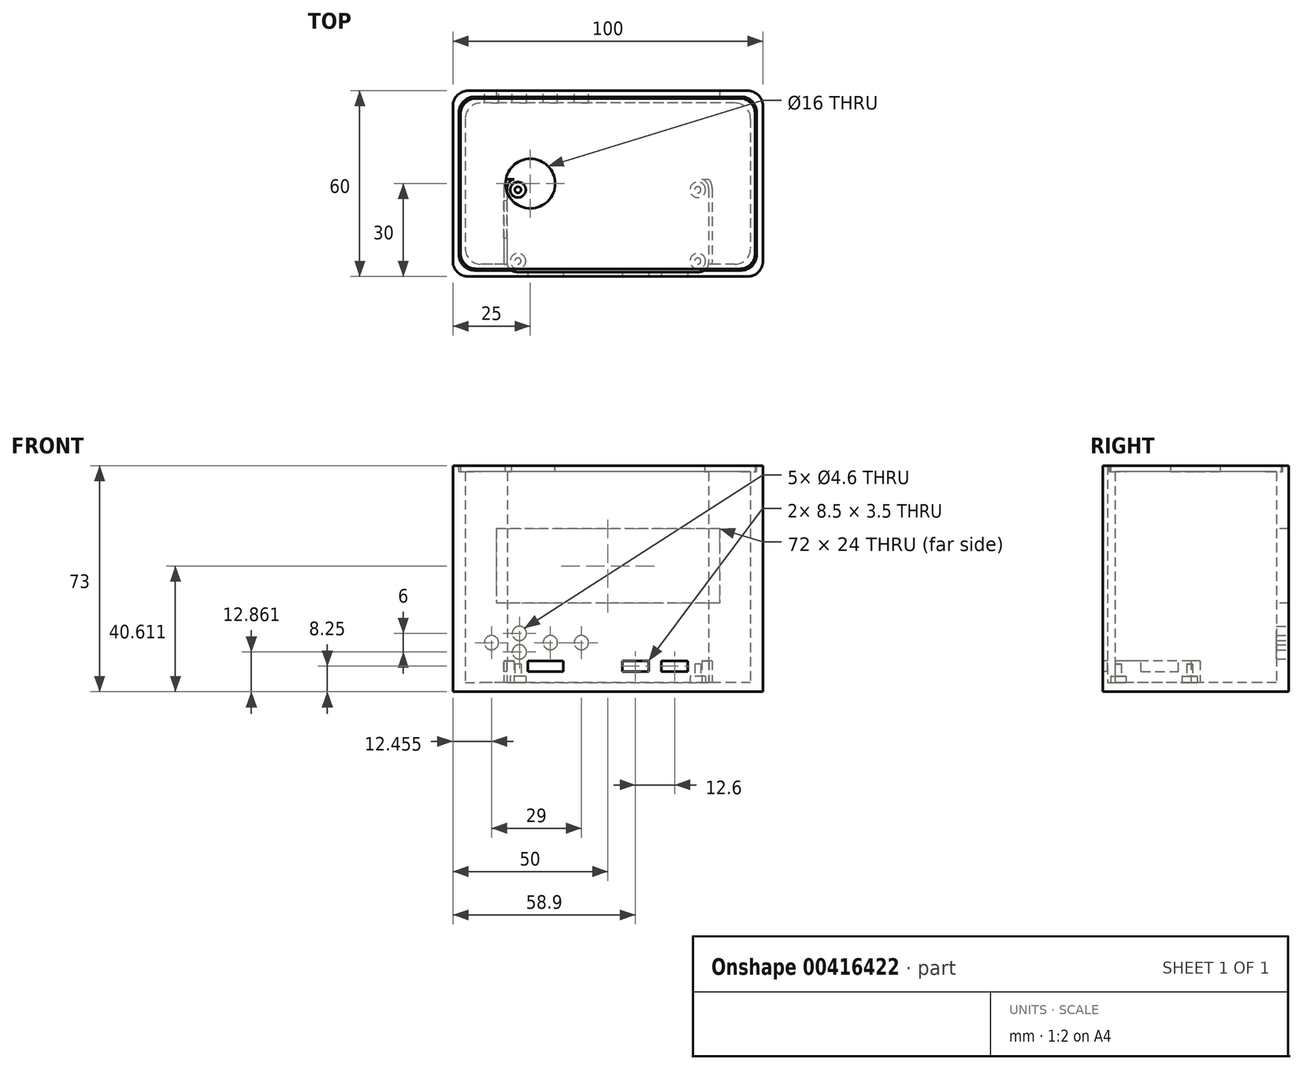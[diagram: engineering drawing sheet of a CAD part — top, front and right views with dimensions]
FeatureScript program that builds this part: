
annotation { "Feature Type Name" : "Feature", "Feature Type Description" : "" }
export const myFeature = defineFeature(function(context is Context, id is Id, definition is map)
    precondition{}
    {
        {
            var Q0;
            Q0=qCreatedBy(makeId("Top.planeOp"),FACE);
            var sketch = newSketch(context, id + "F0", { "sketchPlane" : qUnion([Q0])});
            skLineSegment(sketch, "E0.bottom", {"start": v(45, -30) * mm, "end": v(-45, -30) * mm});
            skLineSegment(sketch, "E0.top", {"start": v(45, 30) * mm, "end": v(-45, 30) * mm});
            skLineSegment(sketch, "E0.left", {"start": v(50, -25) * mm, "end": v(50, 25) * mm});
            skLineSegment(sketch, "E0.right", {"start": v(-50, -25) * mm, "end": v(-50, 25) * mm});
            skPoint(sketch, "E0.middle", {"position": v(0, 0) * mm});
            skPoint(sketch, "E1.visualSharp", {"position": v(-50, -30) * mm});
            skArc(sketch, "E1.filletArc", {"start": v(-50, -25) * mm, "mid": v(-48.54, -28.54) * mm, "end": v(-45, -30) * mm});
            skPoint(sketch, "E2.visualSharp", {"position": v(50, -30) * mm});
            skArc(sketch, "E2.filletArc", {"start": v(45, -30) * mm, "mid": v(48.54, -28.54) * mm, "end": v(50, -25) * mm});
            skPoint(sketch, "E3.visualSharp", {"position": v(50, 30) * mm});
            skArc(sketch, "E3.filletArc", {"start": v(50, 25) * mm, "mid": v(48.54, 28.54) * mm, "end": v(45, 30) * mm});
            skPoint(sketch, "E4.visualSharp", {"position": v(-50, 30) * mm});
            skArc(sketch, "E4.filletArc", {"start": v(-45, 30) * mm, "mid": v(-48.54, 28.54) * mm, "end": v(-50, 25) * mm});
            skSolve(sketch);
        }
        {
            var Q0;
            Q0=makeQuery(id+"F0.imprint","IMPRINT",FACE,{"disambiguationData":[TD([[makeQuery(id+"F0.imprint","IMPRINT",EDGE,{"derivedFrom":sQuery(id+"F0.wireOp",EDGE,"E0.bottom")}),-1.0]])]});
            extrude(context, id + "F1", {"entities" : qUnion([Q0]), "depth" : 3 * mm});
        }
        {
            var Q0;
            Q0=makeQuery(id+"F1.opExtrude","CAP_FACE",FACE,{"disambiguationData":[OSD([sQuery(id+"F0.wireOp",EDGE,"E0.bottom"),sQuery(id+"F0.wireOp",EDGE,"E0.top"),sQuery(id+"F0.wireOp",EDGE,"E0.left"),sQuery(id+"F0.wireOp",EDGE,"E0.right"),sQuery(id+"F0.wireOp",EDGE,"E1.filletArc"),sQuery(id+"F0.wireOp",EDGE,"E2.filletArc"),sQuery(id+"F0.wireOp",EDGE,"E3.filletArc"),sQuery(id+"F0.wireOp",EDGE,"E4.filletArc")])],"isStart":false});
            var sketch = newSketch(context, id + "F2", { "sketchPlane" : qUnion([Q0])});
            skLineSegment(sketch, "E5.rect.bottom", {"start": v(32.5, -28.5) * mm, "end": v(-32.5, -28.5) * mm, "construction": true});
            skLineSegment(sketch, "E5.rect.top", {"start": v(32.5, 1.5) * mm, "end": v(-32.5, 1.5) * mm, "construction": true});
            skLineSegment(sketch, "E5.rect.right", {"start": v(-32.5, -28.5) * mm, "end": v(-32.5, 1.5) * mm, "construction": true});
            skPoint(sketch, "E5.rect.middle", {"position": v(0, -13.5) * mm});
            skLineSegment(sketch, "E6", {"start": v(-20.1, -28.5) * mm, "end": v(-20.1, 1.5) * mm, "construction": true});
            skLineSegment(sketch, "E7", {"start": v(-29, -28.5) * mm, "end": v(-29, 1.5) * mm, "construction": true});
            skLineSegment(sketch, "E8", {"start": v(0, 1.5) * mm, "end": v(0, -28.5) * mm, "construction": true});
            skLineSegment(sketch, "E9.MirrorCS", {"start": v(29, -28.5) * mm, "end": v(29, 1.5) * mm, "construction": true});
            skLineSegment(sketch, "E10", {"start": v(32.5, -13.5) * mm, "end": v(-32.5, -13.5) * mm, "construction": true});
            skLineSegment(sketch, "E11", {"start": v(-32.5, -25) * mm, "end": v(32.5, -25) * mm, "construction": true});
            skLineSegment(sketch, "E12.MirrorCS", {"start": v(-32.5, -2) * mm, "end": v(32.5, -2) * mm, "construction": true});
            skPoint(sketch, "E13", {"position": v(-29, -2) * mm});
            skPoint(sketch, "E14", {"position": v(29, -2) * mm});
            skPoint(sketch, "E15", {"position": v(29, -25) * mm});
            skPoint(sketch, "E16", {"position": v(-29, -25) * mm});
            skLineSegment(sketch, "E17", {"start": v(8.9, 1.5) * mm, "end": v(8.9, -28.5) * mm, "construction": true});
            skLineSegment(sketch, "E18", {"start": v(21.5, 1.5) * mm, "end": v(21.5, -28.5) * mm, "construction": true});
            skArc(sketch, "E19", {"start": v(-32.5, -1.5) * mm, "mid": v(-31.62, 0.62) * mm, "end": v(-29.5, 1.5) * mm});
            skArc(sketch, "E20.MirrorCS", {"start": v(32.5, -1.5) * mm, "mid": v(31.62, 0.62) * mm, "end": v(29.5, 1.5) * mm});
            skArc(sketch, "E21.MirrorCS", {"start": v(-32.5, -25.5) * mm, "mid": v(-31.62, -27.62) * mm, "end": v(-29.5, -28.5) * mm});
            skArc(sketch, "E22.MirrorCS", {"start": v(32.5, -25.5) * mm, "mid": v(31.62, -27.62) * mm, "end": v(29.5, -28.5) * mm});
            skLineSegment(sketch, "E23", {"start": v(-32.5, -1.5) * mm, "end": v(-32.5, -25.5) * mm});
            skLineSegment(sketch, "E24", {"start": v(-29.5, -28.5) * mm, "end": v(29.5, -28.5) * mm});
            skLineSegment(sketch, "E25", {"start": v(-29.5, 1.5) * mm, "end": v(29.5, 1.5) * mm});
            skLineSegment(sketch, "E26", {"start": v(32.5, -1.5) * mm, "end": v(32.5, -25.5) * mm});
            skLineSegment(sketch, "E27", {"start": v(-32.5, -11.6) * mm, "end": v(32.5, -11.6) * mm, "construction": true});
            skArc(sketch, "E28.0", {"start": v(-33.62, -1.5) * mm, "mid": v(-32.3, 1.68) * mm, "end": v(-29.12, 3) * mm});
            skLineSegment(sketch, "E28.1", {"start": v(-33.62, -1.5) * mm, "end": v(-33.62, -25.5) * mm});
            skLineSegment(sketch, "E28.2", {"start": v(-29.12, 3) * mm, "end": v(29.88, 3) * mm});
            skArc(sketch, "E28.3", {"start": v(-33.62, -25.5) * mm, "mid": v(-32.3, -28.68) * mm, "end": v(-29.12, -30) * mm});
            skArc(sketch, "E28.4", {"start": v(33.62, -1.5) * mm, "mid": v(32.58, 1.44) * mm, "end": v(29.88, 3) * mm});
            skLineSegment(sketch, "E28.5", {"start": v(33.62, -1.5) * mm, "end": v(33.62, -25.5) * mm});
            skArc(sketch, "E28.6", {"start": v(33.62, -25.5) * mm, "mid": v(32.3, -28.68) * mm, "end": v(29.12, -30) * mm});
            skLineSegment(sketch, "E28.7", {"start": v(-29.12, -30) * mm, "end": v(29.12, -30) * mm});
            skLineSegment(sketch, "E29.trimOffspring", {"start": v(0, -13.5) * mm, "end": v(0, -30) * mm, "construction": true});
            skSolve(sketch);
        }
        {
            var Q0;
            Q0 = qSketchRegion(id + "F2", true);
            extrude(context, id + "F3", {"entities" : qUnion([Q0]), "operationType" : NewBodyOperationType.ADD, "depth" : 7 * mm});
        }
        {
            var Q0;
            Q0=makeQuery(id+"F3.boolean.opBoolean","MERGE",FACE,{"derivedFrom":[makeQuery(id+"F1.opExtrude","SWEPT_FACE",FACE,{"disambiguationData":[OSD([sQuery(id+"F0.wireOp",EDGE,"E0.bottom")])]}),makeQuery(id+"F3.opExtrude","SWEPT_FACE",FACE,{"disambiguationData":[OSD([sQuery(id+"F2.wireOp",EDGE,"E28.7")])]})]});
            var sketch = newSketch(context, id + "F4", { "sketchPlane" : qUnion([Q0])});
            skPoint(sketch, "E30.0", {"position": v(-20.1, 3) * mm});
            skPoint(sketch, "E30.1", {"position": v(8.9, 3) * mm});
            skPoint(sketch, "E30.2", {"position": v(21.5, 3) * mm});
            skLineSegment(sketch, "E31", {"start": v(-20.1, 3) * mm, "end": v(-20.1, 10.5) * mm, "construction": true});
            skLineSegment(sketch, "E32", {"start": v(8.9, 3) * mm, "end": v(8.9, 10.5) * mm, "construction": true});
            skLineSegment(sketch, "E33", {"start": v(21.5, 3) * mm, "end": v(21.5, 10.5) * mm, "construction": true});
            skLineSegment(sketch, "E34.rect.bottom", {"start": v(-14.35, 6.5) * mm, "end": v(-25.85, 6.5) * mm});
            skLineSegment(sketch, "E34.rect.top", {"start": v(-14.35, 10) * mm, "end": v(-25.85, 10) * mm});
            skLineSegment(sketch, "E34.rect.left", {"start": v(-14.35, 6.5) * mm, "end": v(-14.35, 10) * mm});
            skLineSegment(sketch, "E34.rect.right", {"start": v(-25.85, 6.5) * mm, "end": v(-25.85, 10) * mm});
            skPoint(sketch, "E34.rect.middle", {"position": v(-20.1, 8.25) * mm});
            skLineSegment(sketch, "E35.rect.bottom", {"start": v(13.15, 6.5) * mm, "end": v(4.65, 6.5) * mm});
            skLineSegment(sketch, "E35.rect.top", {"start": v(13.15, 10) * mm, "end": v(4.65, 10) * mm});
            skLineSegment(sketch, "E35.rect.left", {"start": v(13.15, 6.5) * mm, "end": v(13.15, 10) * mm});
            skLineSegment(sketch, "E35.rect.right", {"start": v(4.65, 6.5) * mm, "end": v(4.65, 10) * mm});
            skPoint(sketch, "E35.rect.middle", {"position": v(8.9, 8.25) * mm});
            skLineSegment(sketch, "E36.rect.bottom", {"start": v(25.75, 6.5) * mm, "end": v(17.25, 6.5) * mm});
            skLineSegment(sketch, "E36.rect.top", {"start": v(25.75, 10) * mm, "end": v(17.25, 10) * mm});
            skLineSegment(sketch, "E36.rect.left", {"start": v(25.75, 6.5) * mm, "end": v(25.75, 10) * mm});
            skLineSegment(sketch, "E36.rect.right", {"start": v(17.25, 6.5) * mm, "end": v(17.25, 10) * mm});
            skPoint(sketch, "E36.rect.middle", {"position": v(21.5, 8.25) * mm});
            skSolve(sketch);
        }
        {
            var Q0;
            Q0 = qSketchRegion(id + "F4", true);
            extrude(context, id + "F5", {"entities" : qUnion([Q0]), "operationType" : NewBodyOperationType.REMOVE, "endBound" : BoundingType.UP_TO_NEXT, "oppositeDirection" : true, "depth" : 25 * mm});
        }
        {
            var Q0;
            Q0=makeQuery(id+"F2.imprint","IMPRINT",FACE,{"disambiguationData":[TD([[makeQuery(id+"F2.imprint","IMPRINT",EDGE,{"derivedFrom":sQuery(id+"F2.wireOp",EDGE,"E19")}),-1.0]])]});
            var sketch = newSketch(context, id + "F6", { "sketchPlane" : qUnion([Q0])});
            skPoint(sketch, "E37.0", {"position": v(-29, -2) * mm});
            skCircle(sketch, "E38", {"center": v(-29, -2) * mm, "radius": 2.5 * mm});
            skCircle(sketch, "E39.MirrorC", {"center": v(29, -2) * mm, "radius": 2.5 * mm});
            skCircle(sketch, "E40.MirrorC", {"center": v(29, -25) * mm, "radius": 2.5 * mm});
            skCircle(sketch, "E41.MirrorC", {"center": v(-29, -25) * mm, "radius": 2.5 * mm});
            skSolve(sketch);
        }
        {
            var Q0;
            Q0 = qSketchRegion(id + "F6", true);
            extrude(context, id + "F7", {"entities" : qUnion([Q0]), "operationType" : NewBodyOperationType.ADD, "depth" : 2 * mm});
        }
        {
            var Q0;
            Q0=makeQuery(id+"F7.opExtrude","CAP_FACE",FACE,{"disambiguationData":[OSD([sQuery(id+"F6.wireOp",EDGE,"E38")])],"isStart":false});
            var sketch = newSketch(context, id + "F8", { "sketchPlane" : qUnion([Q0])});
            skPoint(sketch, "E42.0", {"position": v(-29, -2) * mm});
            skCircle(sketch, "E43", {"center": v(-29, -2) * mm, "radius": 1 * mm});
            skCircle(sketch, "E44.MirrorC", {"center": v(29, -2) * mm, "radius": 1 * mm});
            skCircle(sketch, "E45.MirrorC", {"center": v(29, -25) * mm, "radius": 1 * mm});
            skCircle(sketch, "E46.MirrorC", {"center": v(-29, -25) * mm, "radius": 1 * mm});
            skSolve(sketch);
        }
        {
            var Q0;
            Q0 = qSketchRegion(id + "F8", true);
            extrude(context, id + "F9", {"entities" : qUnion([Q0]), "operationType" : NewBodyOperationType.ADD, "depth" : 4 * mm});
        }
        {
            var Q0;
            Q0=makeQuery(id+"F3.opExtrude","SWEPT_FACE",FACE,{"disambiguationData":[OSD([sQuery(id+"F2.wireOp",EDGE,"E28.1")])]});
            var sketch = newSketch(context, id + "F10", { "sketchPlane" : qUnion([Q0])});
            skPoint(sketch, "E47.0", {"position": v(11.6, 3) * mm});
            skLineSegment(sketch, "E48", {"start": v(11.6, 3) * mm, "end": v(11.6, 11.3) * mm, "construction": true});
            skLineSegment(sketch, "E49.rect.bottom", {"start": v(17.65, 6.5) * mm, "end": v(5.55, 6.5) * mm});
            skLineSegment(sketch, "E49.rect.top", {"start": v(17.65, 10) * mm, "end": v(5.55, 10) * mm});
            skLineSegment(sketch, "E49.rect.left", {"start": v(17.65, 6.5) * mm, "end": v(17.65, 10) * mm});
            skLineSegment(sketch, "E49.rect.right", {"start": v(5.55, 6.5) * mm, "end": v(5.55, 10) * mm});
            skPoint(sketch, "E49.rect.middle", {"position": v(11.6, 8.25) * mm});
            skSolve(sketch);
        }
        {
            var Q0;
            Q0 = qSketchRegion(id + "F10", true);
            extrude(context, id + "F11", {"entities" : qUnion([Q0]), "operationType" : NewBodyOperationType.REMOVE, "endBound" : BoundingType.UP_TO_NEXT, "oppositeDirection" : true, "depth" : 25 * mm});
        }
        {
            var Q0;
            Q0=makeQuery(id+"F2.imprint","IMPRINT",FACE,{"disambiguationData":[TD([[makeQuery(id+"F2.imprint","IMPRINT",EDGE,{"derivedFrom":sQuery(id+"F2.wireOp",EDGE,"E28.0")}),1.0]])]});
            var sketch = newSketch(context, id + "F12", { "sketchPlane" : qUnion([Q0])});
            skLineSegment(sketch, "E50.bottom", {"start": v(45, 30) * mm, "end": v(-45, 30) * mm});
            skLineSegment(sketch, "E50.top", {"start": v(45, -30) * mm, "end": v(29.12, -30) * mm});
            skLineSegment(sketch, "E50.left", {"start": v(50, 25) * mm, "end": v(50, -25) * mm});
            skLineSegment(sketch, "E50.right", {"start": v(-50, 25) * mm, "end": v(-50, -25) * mm});
            skPoint(sketch, "E50.middle", {"position": v(0, 0) * mm});
            skPoint(sketch, "E51.visualSharp", {"position": v(50, 30) * mm});
            skArc(sketch, "E51.filletArc", {"start": v(50, 25) * mm, "mid": v(48.54, 28.54) * mm, "end": v(45, 30) * mm});
            skPoint(sketch, "E52.visualSharp", {"position": v(50, -30) * mm});
            skArc(sketch, "E52.filletArc", {"start": v(45, -30) * mm, "mid": v(48.54, -28.54) * mm, "end": v(50, -25) * mm});
            skPoint(sketch, "E53.visualSharp", {"position": v(-50, -30) * mm});
            skArc(sketch, "E53.filletArc", {"start": v(-50, -25) * mm, "mid": v(-48.54, -28.54) * mm, "end": v(-45, -30) * mm});
            skPoint(sketch, "E54.visualSharp", {"position": v(-50, 30) * mm});
            skArc(sketch, "E54.filletArc", {"start": v(-45, 30) * mm, "mid": v(-48.54, 28.54) * mm, "end": v(-50, 25) * mm});
            skLineSegment(sketch, "E55.bottom", {"start": v(41, 26) * mm, "end": v(-41, 26) * mm});
            skLineSegment(sketch, "E55.top", {"start": v(41, -26) * mm, "end": v(33.6, -26) * mm});
            skLineSegment(sketch, "E55.left", {"start": v(46, 21) * mm, "end": v(46, -21) * mm});
            skLineSegment(sketch, "E55.right", {"start": v(-46, 21) * mm, "end": v(-46, -21) * mm});
            skPoint(sketch, "E56.visualSharp", {"position": v(46, 26) * mm});
            skArc(sketch, "E56.filletArc", {"start": v(46, 21) * mm, "mid": v(44.54, 24.54) * mm, "end": v(41, 26) * mm});
            skPoint(sketch, "E57.visualSharp", {"position": v(46, -26) * mm});
            skArc(sketch, "E57.filletArc", {"start": v(41, -26) * mm, "mid": v(44.54, -24.54) * mm, "end": v(46, -21) * mm});
            skPoint(sketch, "E58.visualSharp", {"position": v(-46, -26) * mm});
            skArc(sketch, "E58.filletArc", {"start": v(-46, -21) * mm, "mid": v(-44.54, -24.54) * mm, "end": v(-41, -26) * mm});
            skPoint(sketch, "E59.visualSharp", {"position": v(-46, 26) * mm});
            skArc(sketch, "E59.filletArc", {"start": v(-41, 26) * mm, "mid": v(-44.54, 24.54) * mm, "end": v(-46, 21) * mm});
            skLineSegment(sketch, "E60.trimOffspring", {"start": v(-29.12, -30) * mm, "end": v(-45, -30) * mm});
            skLineSegment(sketch, "E61.trimOffspring", {"start": v(-33.6, -26) * mm, "end": v(-41, -26) * mm});
            skArc(sketch, "E62.0", {"start": v(-33.6, -26) * mm, "mid": v(-32.12, -28.85) * mm, "end": v(-29.12, -30) * mm});
            skArc(sketch, "E63.0", {"start": v(33.6, -26) * mm, "mid": v(32.12, -28.85) * mm, "end": v(29.12, -30) * mm});
            skPoint(sketch, "E64.orphan", {"position": v(33.62, -25.5) * mm});
            skPoint(sketch, "E65.orphan", {"position": v(-33.62, -25.5) * mm});
            skSolve(sketch);
        }
        {
            var Q0;
            Q0 = qSketchRegion(id + "F12", true);
            var Q1;
            {var subQ0=sQuery(id+"F2.wireOp",EDGE,"E23");var subQ2=sQuery(id+"F2.wireOp",EDGE,"E28.7");var subQ4=sQuery(id+"F2.wireOp",EDGE,"E21.MirrorCS");var subQ5=makeQuery(id+"F3.opExtrude","SWEPT_FACE",FACE,{"disambiguationData":[OSD([subQ4])]});var subQ6=sQuery(id+"F2.wireOp",EDGE,"E24");var subQ9=sQuery(id+"F2.wireOp",EDGE,"E28.1");var subQ12=sQuery(id+"F2.wireOp",EDGE,"E28.3");var subQ14=sQuery(id+"F2.wireOp",EDGE,"E26");var subQ15=sQuery(id+"F2.wireOp",EDGE,"E25");var subQ16=sQuery(id+"F2.wireOp",EDGE,"E22.MirrorCS");var subQ17=sQuery(id+"F2.wireOp",EDGE,"E28.0");var subQ18=sQuery(id+"F2.wireOp",EDGE,"E19");var subQ19=sQuery(id+"F2.wireOp",EDGE,"E20.MirrorCS");var subQ20=sQuery(id+"F2.wireOp",EDGE,"E28.2");var subQ21=sQuery(id+"F2.wireOp",EDGE,"E28.4");var subQ22=sQuery(id+"F2.wireOp",EDGE,"E28.5");var subQ23=sQuery(id+"F2.wireOp",EDGE,"E28.6");Q1=makeQuery(id+"F11.boolean.opBoolean","SPLIT",FACE,{"disambiguationData":[TD([subQ5])],"derivedFrom":makeQuery(id+"F5.boolean.opBoolean","SPLIT",FACE,{"disambiguationData":[TD([makeQuery(id+"F3.opExtrude","SWEPT_FACE",FACE,{"disambiguationData":[OSD([subQ18])]})])],"derivedFrom":makeQuery(id+"F3.opExtrude","CAP_FACE",FACE,{"disambiguationData":[OSD([subQ18,subQ19,subQ4,subQ16,subQ0,subQ6,subQ15,subQ14,subQ17,subQ9,subQ20,subQ12,subQ21,subQ22,subQ23,subQ2])],"isStart":false})})});}
            extrude(context, id + "F13", {"entities" : qUnion([Q0]), "operationType" : NewBodyOperationType.ADD, "endBound" : BoundingType.UP_TO_SURFACE, "endBoundEntityFace" : qUnion([Q1]), "depth" : 66 * mm});
        }
        {
            var Q0;
            {var subQ0=sQuery(id+"F2.wireOp",EDGE,"E23");var subQ2=sQuery(id+"F2.wireOp",EDGE,"E28.7");var subQ4=sQuery(id+"F2.wireOp",EDGE,"E21.MirrorCS");var subQ5=makeQuery(id+"F3.opExtrude","SWEPT_FACE",FACE,{"disambiguationData":[OSD([subQ4])]});var subQ6=sQuery(id+"F2.wireOp",EDGE,"E24");var subQ9=sQuery(id+"F2.wireOp",EDGE,"E28.1");var subQ12=sQuery(id+"F2.wireOp",EDGE,"E28.3");var subQ14=sQuery(id+"F2.wireOp",EDGE,"E26");var subQ16=sQuery(id+"F2.wireOp",EDGE,"E25");var subQ18=sQuery(id+"F2.wireOp",EDGE,"E22.MirrorCS");var subQ20=sQuery(id+"F2.wireOp",EDGE,"E28.0");var subQ22=sQuery(id+"F2.wireOp",EDGE,"E19");var subQ23=makeQuery(id+"F3.opExtrude","SWEPT_FACE",FACE,{"disambiguationData":[OSD([subQ22])]});var subQ24=sQuery(id+"F2.wireOp",EDGE,"E20.MirrorCS");var subQ27=sQuery(id+"F2.wireOp",EDGE,"E28.2");var subQ29=sQuery(id+"F2.wireOp",EDGE,"E28.4");var subQ31=sQuery(id+"F2.wireOp",EDGE,"E28.5");var subQ33=sQuery(id+"F2.wireOp",EDGE,"E28.6");var subQ35=makeQuery(id+"F5.boolean.opBoolean","SPLIT",FACE,{"disambiguationData":[TD([subQ23])],"derivedFrom":makeQuery(id+"F3.opExtrude","CAP_FACE",FACE,{"disambiguationData":[OSD([subQ22,subQ24,subQ4,subQ18,subQ0,subQ6,subQ16,subQ14,subQ20,subQ9,subQ27,subQ12,subQ29,subQ31,subQ33,subQ2])],"isStart":false})});Q0=makeQuery(id+"F13.boolean.opBoolean","MERGE",FACE,{"derivedFrom":[makeQuery(id+"F11.boolean.opBoolean","SPLIT",FACE,{"disambiguationData":[TD([subQ23])],"derivedFrom":subQ35}),makeQuery(id+"F11.boolean.opBoolean","SPLIT",FACE,{"disambiguationData":[TD([subQ5])],"derivedFrom":subQ35}),makeQuery(id+"F13.opExtrude","CAP_FACE",FACE,{"disambiguationData":[OSD([sQuery(id+"F12.wireOp",EDGE,"E50.bottom"),sQuery(id+"F12.wireOp",EDGE,"E50.top"),sQuery(id+"F12.wireOp",EDGE,"E50.left"),sQuery(id+"F12.wireOp",EDGE,"E50.right"),sQuery(id+"F12.wireOp",EDGE,"E51.filletArc"),sQuery(id+"F12.wireOp",EDGE,"E52.filletArc"),sQuery(id+"F12.wireOp",EDGE,"E53.filletArc"),sQuery(id+"F12.wireOp",EDGE,"E54.filletArc"),sQuery(id+"F12.wireOp",EDGE,"E55.bottom"),sQuery(id+"F12.wireOp",EDGE,"E55.top"),sQuery(id+"F12.wireOp",EDGE,"E55.left"),sQuery(id+"F12.wireOp",EDGE,"E55.right"),sQuery(id+"F12.wireOp",EDGE,"E56.filletArc"),sQuery(id+"F12.wireOp",EDGE,"E57.filletArc"),sQuery(id+"F12.wireOp",EDGE,"E58.filletArc"),sQuery(id+"F12.wireOp",EDGE,"E59.filletArc"),sQuery(id+"F12.wireOp",EDGE,"E60.trimOffspring"),sQuery(id+"F12.wireOp",EDGE,"E61.trimOffspring"),sQuery(id+"F12.wireOp",EDGE,"E62.0"),sQuery(id+"F12.wireOp",EDGE,"E63.0")])],"isStart":false})]});}
            var sketch = newSketch(context, id + "F14", { "sketchPlane" : qUnion([Q0])});
            skLineSegment(sketch, "E66.bottom", {"start": v(45, 30) * mm, "end": v(-45, 30) * mm});
            skLineSegment(sketch, "E66.top", {"start": v(45, -30) * mm, "end": v(-45, -30) * mm});
            skLineSegment(sketch, "E66.left", {"start": v(50, 25) * mm, "end": v(50, -25) * mm});
            skLineSegment(sketch, "E66.right", {"start": v(-50, 25) * mm, "end": v(-50, -25) * mm});
            skPoint(sketch, "E66.middle", {"position": v(0, 0) * mm});
            skPoint(sketch, "E67.visualSharp", {"position": v(50, 30) * mm});
            skArc(sketch, "E67.filletArc", {"start": v(50, 25) * mm, "mid": v(48.54, 28.54) * mm, "end": v(45, 30) * mm});
            skPoint(sketch, "E68.visualSharp", {"position": v(-50, 30) * mm});
            skArc(sketch, "E68.filletArc", {"start": v(-45, 30) * mm, "mid": v(-48.54, 28.54) * mm, "end": v(-50, 25) * mm});
            skPoint(sketch, "E69.visualSharp", {"position": v(-50, -30) * mm});
            skArc(sketch, "E69.filletArc", {"start": v(-50, -25) * mm, "mid": v(-48.54, -28.54) * mm, "end": v(-45, -30) * mm});
            skPoint(sketch, "E70.visualSharp", {"position": v(50, -30) * mm});
            skArc(sketch, "E70.filletArc", {"start": v(45, -30) * mm, "mid": v(48.54, -28.54) * mm, "end": v(50, -25) * mm});
            skLineSegment(sketch, "E71.bottom", {"start": v(41, 26) * mm, "end": v(-41, 26) * mm});
            skLineSegment(sketch, "E71.left", {"start": v(46, 21) * mm, "end": v(46, -21) * mm});
            skLineSegment(sketch, "E71.right", {"start": v(-46, 21) * mm, "end": v(-46, -21) * mm});
            skPoint(sketch, "E72.visualSharp", {"position": v(46, 26) * mm});
            skArc(sketch, "E72.filletArc", {"start": v(46, 21) * mm, "mid": v(44.54, 24.54) * mm, "end": v(41, 26) * mm});
            skPoint(sketch, "E73.visualSharp", {"position": v(46, -26) * mm});
            skArc(sketch, "E73.filletArc", {"start": v(41, -26) * mm, "mid": v(44.54, -24.54) * mm, "end": v(46, -21) * mm});
            skPoint(sketch, "E74.visualSharp", {"position": v(-46, -26) * mm});
            skArc(sketch, "E74.filletArc", {"start": v(-46, -21) * mm, "mid": v(-44.54, -24.54) * mm, "end": v(-41, -26) * mm});
            skPoint(sketch, "E75.visualSharp", {"position": v(-46, 26) * mm});
            skArc(sketch, "E75.filletArc", {"start": v(-41, 26) * mm, "mid": v(-44.54, 24.54) * mm, "end": v(-46, 21) * mm});
            skArc(sketch, "E76", {"start": v(-32.46, -26) * mm, "mid": v(-31.44, -27.8) * mm, "end": v(-29.5, -28.5) * mm});
            skArc(sketch, "E77", {"start": v(29.5, -28.5) * mm, "mid": v(31.44, -27.8) * mm, "end": v(32.46, -26) * mm});
            skLineSegment(sketch, "E78", {"start": v(41, -26) * mm, "end": v(32.46, -26) * mm});
            skLineSegment(sketch, "E79", {"start": v(29.5, -28.5) * mm, "end": v(-29.5, -28.5) * mm});
            skLineSegment(sketch, "E80", {"start": v(-41, -26) * mm, "end": v(-32.46, -26) * mm});
            skSolve(sketch);
        }
        {
            var Q0;
            Q0 = qSketchRegion(id + "F14", true);
            extrude(context, id + "F15", {"entities" : qUnion([Q0]), "operationType" : NewBodyOperationType.ADD, "depth" : 63 * mm});
        }
        {
            var Q0;
            Q0=makeQuery(id+"F15.opExtrude","CAP_FACE",FACE,{"disambiguationData":[OSD([sQuery(id+"F14.wireOp",EDGE,"E66.bottom"),sQuery(id+"F14.wireOp",EDGE,"E66.top"),sQuery(id+"F14.wireOp",EDGE,"E66.left"),sQuery(id+"F14.wireOp",EDGE,"E66.right"),sQuery(id+"F14.wireOp",EDGE,"E67.filletArc"),sQuery(id+"F14.wireOp",EDGE,"E68.filletArc"),sQuery(id+"F14.wireOp",EDGE,"E69.filletArc"),sQuery(id+"F14.wireOp",EDGE,"E70.filletArc"),sQuery(id+"F14.wireOp",EDGE,"E71.bottom"),sQuery(id+"F14.wireOp",EDGE,"E71.left"),sQuery(id+"F14.wireOp",EDGE,"E71.right"),sQuery(id+"F14.wireOp",EDGE,"E72.filletArc"),sQuery(id+"F14.wireOp",EDGE,"E73.filletArc"),sQuery(id+"F14.wireOp",EDGE,"E74.filletArc"),sQuery(id+"F14.wireOp",EDGE,"E75.filletArc"),sQuery(id+"F14.wireOp",EDGE,"E76"),sQuery(id+"F14.wireOp",EDGE,"E77"),sQuery(id+"F14.wireOp",EDGE,"E78"),sQuery(id+"F14.wireOp",EDGE,"E79"),sQuery(id+"F14.wireOp",EDGE,"E80")])],"isStart":false});
            var sketch = newSketch(context, id + "F16", { "sketchPlane" : qUnion([Q0])});
            skLineSegment(sketch, "E81.bottom", {"start": v(43, 28) * mm, "end": v(-43, 28) * mm});
            skLineSegment(sketch, "E81.top", {"start": v(43, -28) * mm, "end": v(-43, -28) * mm});
            skLineSegment(sketch, "E81.left", {"start": v(48, 23) * mm, "end": v(48, -23) * mm});
            skLineSegment(sketch, "E81.right", {"start": v(-48, 23) * mm, "end": v(-48, -23) * mm});
            skPoint(sketch, "E81.middle", {"position": v(0, 0) * mm});
            skPoint(sketch, "E82.visualSharp", {"position": v(-48, -28) * mm});
            skArc(sketch, "E82.filletArc", {"start": v(-48, -23) * mm, "mid": v(-46.54, -26.54) * mm, "end": v(-43, -28) * mm});
            skPoint(sketch, "E83.visualSharp", {"position": v(48, -28) * mm});
            skArc(sketch, "E83.filletArc", {"start": v(43, -28) * mm, "mid": v(46.54, -26.54) * mm, "end": v(48, -23) * mm});
            skPoint(sketch, "E84.visualSharp", {"position": v(48, 28) * mm});
            skArc(sketch, "E84.filletArc", {"start": v(48, 23) * mm, "mid": v(46.54, 26.54) * mm, "end": v(43, 28) * mm});
            skPoint(sketch, "E85.visualSharp", {"position": v(-48, 28) * mm});
            skArc(sketch, "E85.filletArc", {"start": v(-43, 28) * mm, "mid": v(-46.54, 26.54) * mm, "end": v(-48, 23) * mm});
            skSolve(sketch);
        }
        {
            var Q0;
            Q0 = qSketchRegion(id + "F16", true);
            extrude(context, id + "F17", {"entities" : qUnion([Q0]), "operationType" : NewBodyOperationType.REMOVE, "oppositeDirection" : true, "depth" : 2 * mm});
        }
        {
            var Q0;
            Q0=makeQuery(id+"F15.boolean.opBoolean","MERGE",FACE,{"derivedFrom":[makeQuery(id+"F13.opExtrude","SWEPT_FACE",FACE,{"disambiguationData":[OSD([sQuery(id+"F12.wireOp",EDGE,"E55.bottom")])]}),makeQuery(id+"F15.opExtrude","SWEPT_FACE",FACE,{"disambiguationData":[OSD([sQuery(id+"F14.wireOp",EDGE,"E71.bottom")])]})]});
            var sketch = newSketch(context, id + "F18", { "sketchPlane" : qUnion([Q0])});
            skLineSegment(sketch, "E86.bottom", {"start": v(37.47, 56.1) * mm, "end": v(-37.47, 56.1) * mm, "construction": true});
            skLineSegment(sketch, "E86.top", {"start": v(37.47, 25.12) * mm, "end": v(-37.47, 25.12) * mm, "construction": true});
            skLineSegment(sketch, "E86.left", {"start": v(37.47, 56.1) * mm, "end": v(37.47, 25.12) * mm, "construction": true});
            skLineSegment(sketch, "E86.right", {"start": v(-37.47, 56.1) * mm, "end": v(-37.47, 25.12) * mm, "construction": true});
            skPoint(sketch, "E86.middle", {"position": v(0, 40.61) * mm});
            skCircle(sketch, "E87", {"center": v(-37.47, 56.1) * mm, "radius": 3 * mm});
            skCircle(sketch, "E88", {"center": v(37.47, 56.1) * mm, "radius": 3 * mm});
            skCircle(sketch, "E89", {"center": v(37.47, 25.12) * mm, "radius": 3 * mm});
            skCircle(sketch, "E90", {"center": v(-37.47, 25.12) * mm, "radius": 3 * mm});
            skCircle(sketch, "E91", {"center": v(-37.47, 56.1) * mm, "radius": 1.13 * mm});
            skCircle(sketch, "E92", {"center": v(37.47, 56.1) * mm, "radius": 1.13 * mm});
            skCircle(sketch, "E93", {"center": v(37.47, 25.12) * mm, "radius": 1.13 * mm});
            skCircle(sketch, "E94", {"center": v(-37.47, 25.12) * mm, "radius": 1.13 * mm});
            skSolve(sketch);
        }
        {
            var Q0;
            Q0=makeQuery(id+"FcJJ7sOJFXP5bAi_1.boolean.opBoolean","SPLIT",FACE,{"disambiguationData":[TD([makeQuery(id+"F13.opExtrude","SWEPT_FACE",FACE,{"disambiguationData":[OSD([sQuery(id+"F12.wireOp",EDGE,"E56.filletArc")])]})])],"derivedFrom":makeQuery(id+"F15.boolean.opBoolean","MERGE",FACE,{"derivedFrom":[makeQuery(id+"F13.opExtrude","SWEPT_FACE",FACE,{"disambiguationData":[OSD([sQuery(id+"F12.wireOp",EDGE,"E55.bottom")])]}),makeQuery(id+"F15.opExtrude","SWEPT_FACE",FACE,{"disambiguationData":[OSD([sQuery(id+"F14.wireOp",EDGE,"E71.bottom")])]})]})});
            var sketch = newSketch(context, id + "F19", { "sketchPlane" : qUnion([Q0])});
            skLineSegment(sketch, "E95", {"start": v(-37.47, 56.1) * mm, "end": v(37.47, 25.12) * mm, "construction": true});
            skLineSegment(sketch, "E96", {"start": v(37.47, 25.12) * mm, "end": v(37.47, 56.1) * mm, "construction": true});
            skLineSegment(sketch, "E97", {"start": v(37.47, 56.1) * mm, "end": v(-37.47, 25.12) * mm, "construction": true});
            skLineSegment(sketch, "E98", {"start": v(-37.47, 25.12) * mm, "end": v(37.47, 25.12) * mm, "construction": true});
            skLineSegment(sketch, "E99", {"start": v(0, 25.12) * mm, "end": v(0, 40.61) * mm, "construction": true});
            skLineSegment(sketch, "E100.bottom", {"start": v(36, 52.61) * mm, "end": v(-36, 52.61) * mm});
            skLineSegment(sketch, "E100.top", {"start": v(36, 28.61) * mm, "end": v(-36, 28.61) * mm});
            skLineSegment(sketch, "E100.left", {"start": v(36, 52.61) * mm, "end": v(36, 28.61) * mm});
            skLineSegment(sketch, "E100.right", {"start": v(-36, 52.61) * mm, "end": v(-36, 28.61) * mm});
            skPoint(sketch, "E100.middle", {"position": v(0, 40.61) * mm});
            skSolve(sketch);
        }
        {
            var Q0;
            Q0 = qSketchRegion(id + "F19", true);
            extrude(context, id + "F20", {"entities" : qUnion([Q0]), "operationType" : NewBodyOperationType.REMOVE, "endBound" : BoundingType.UP_TO_NEXT, "oppositeDirection" : true, "depth" : 25 * mm});
        }
        {
            var Q0;
            Q0=makeQuery(id+"F15.boolean.opBoolean","MERGE",FACE,{"derivedFrom":[makeQuery(id+"F13.boolean.opBoolean","MERGE",FACE,{"derivedFrom":[makeQuery(id+"F1.opExtrude","SWEPT_FACE",FACE,{"disambiguationData":[OSD([sQuery(id+"F0.wireOp",EDGE,"E0.top")])]}),makeQuery(id+"F13.opExtrude","SWEPT_FACE",FACE,{"disambiguationData":[OSD([sQuery(id+"F12.wireOp",EDGE,"E50.bottom")])]})]}),makeQuery(id+"F15.opExtrude","SWEPT_FACE",FACE,{"disambiguationData":[OSD([sQuery(id+"F14.wireOp",EDGE,"E66.bottom")])]})]});
            var sketch = newSketch(context, id + "F21", { "sketchPlane" : qUnion([Q0])});
            skCircle(sketch, "E101", {"center": v(8.54, 15.86) * mm, "radius": 2.3 * mm});
            skCircle(sketch, "E102", {"center": v(18.54, 15.86) * mm, "radius": 2.3 * mm});
            skCircle(sketch, "E103", {"center": v(28.55, 12.86) * mm, "radius": 2.3 * mm});
            skCircle(sketch, "E104", {"center": v(28.55, 18.86) * mm, "radius": 2.3 * mm});
            skCircle(sketch, "E105", {"center": v(37.55, 15.86) * mm, "radius": 2.3 * mm});
            skLineSegment(sketch, "E106.bottom", {"start": v(42.54, 65) * mm, "end": v(-42.55, 65) * mm, "construction": true});
            skLineSegment(sketch, "E106.top", {"start": v(42.54, 8.86) * mm, "end": v(-42.55, 8.86) * mm, "construction": true});
            skLineSegment(sketch, "E106.left", {"start": v(42.54, 65) * mm, "end": v(42.54, 8.86) * mm, "construction": true});
            skLineSegment(sketch, "E106.right", {"start": v(-42.55, 65) * mm, "end": v(-42.55, 8.86) * mm, "construction": true});
            skPoint(sketch, "E106.middle", {"position": v(0, 36.93) * mm});
            skCircle(sketch, "E107", {"center": v(-37.47, 56.1) * mm, "radius": 1.52 * mm, "construction": true});
            skCircle(sketch, "E108", {"center": v(37.46, 56.1) * mm, "radius": 1.52 * mm, "construction": true});
            skCircle(sketch, "E109", {"center": v(-37.46, 25.12) * mm, "radius": 1.52 * mm, "construction": true});
            skCircle(sketch, "E110", {"center": v(37.46, 25.12) * mm, "radius": 1.52 * mm, "construction": true});
            skSolve(sketch);
        }
        {
            var Q0;
            Q0 = qSketchRegion(id + "F21", true);
            extrude(context, id + "F22", {"entities" : qUnion([Q0]), "operationType" : NewBodyOperationType.REMOVE, "endBound" : BoundingType.UP_TO_NEXT, "oppositeDirection" : true, "depth" : 25 * mm});
        }
        {
            var Q0;
            {var subQ0=sQuery(id+"F2.wireOp",EDGE,"E28.2");var subQ2=sQuery(id+"F2.wireOp",EDGE,"E28.0");var subQ4=sQuery(id+"F2.wireOp",EDGE,"E26");var subQ6=sQuery(id+"F2.wireOp",EDGE,"E25");var subQ8=sQuery(id+"F2.wireOp",EDGE,"E28.1");var subQ10=sQuery(id+"F2.wireOp",EDGE,"E19");var subQ11=makeQuery(id+"F3.opExtrude","SWEPT_FACE",FACE,{"disambiguationData":[OSD([subQ10])]});var subQ12=sQuery(id+"F2.wireOp",EDGE,"E22.MirrorCS");var subQ14=sQuery(id+"F2.wireOp",EDGE,"E28.4");var subQ16=sQuery(id+"F2.wireOp",EDGE,"E20.MirrorCS");var subQ18=sQuery(id+"F2.wireOp",EDGE,"E23");var subQ20=sQuery(id+"F2.wireOp",EDGE,"E28.5");var subQ22=sQuery(id+"F2.wireOp",EDGE,"E28.6");var subQ25=sQuery(id+"F12.wireOp",EDGE,"E55.top");var subQ26=sQuery(id+"F2.wireOp",EDGE,"E28.7");var subQ28=sQuery(id+"F2.wireOp",EDGE,"E21.MirrorCS");var subQ29=makeQuery(id+"F3.opExtrude","SWEPT_FACE",FACE,{"disambiguationData":[OSD([subQ28])]});var subQ30=sQuery(id+"F2.wireOp",EDGE,"E24");var subQ34=sQuery(id+"F2.wireOp",EDGE,"E28.3");var subQ37=makeQuery(id+"F5.boolean.opBoolean","SPLIT",FACE,{"disambiguationData":[TD([subQ11])],"derivedFrom":makeQuery(id+"F3.opExtrude","CAP_FACE",FACE,{"disambiguationData":[OSD([subQ10,subQ16,subQ28,subQ12,subQ18,subQ30,subQ6,subQ4,subQ2,subQ8,subQ0,subQ34,subQ14,subQ20,subQ22,subQ26])],"isStart":false})});Q0=makeQuery(id+"F15.boolean.opBoolean","SPLIT",FACE,{"disambiguationData":[TD([subQ11])],"derivedFrom":makeQuery(id+"F13.boolean.opBoolean","MERGE",FACE,{"derivedFrom":[makeQuery(id+"F11.boolean.opBoolean","SPLIT",FACE,{"disambiguationData":[TD([subQ11])],"derivedFrom":subQ37}),makeQuery(id+"F11.boolean.opBoolean","SPLIT",FACE,{"disambiguationData":[TD([subQ29])],"derivedFrom":subQ37}),makeQuery(id+"F13.opExtrude","CAP_FACE",FACE,{"disambiguationData":[OSD([sQuery(id+"F12.wireOp",EDGE,"E50.bottom"),sQuery(id+"F12.wireOp",EDGE,"E50.top"),sQuery(id+"F12.wireOp",EDGE,"E50.left"),sQuery(id+"F12.wireOp",EDGE,"E50.right"),sQuery(id+"F12.wireOp",EDGE,"E51.filletArc"),sQuery(id+"F12.wireOp",EDGE,"E52.filletArc"),sQuery(id+"F12.wireOp",EDGE,"E53.filletArc"),sQuery(id+"F12.wireOp",EDGE,"E54.filletArc"),sQuery(id+"F12.wireOp",EDGE,"E55.bottom"),subQ25,sQuery(id+"F12.wireOp",EDGE,"E55.left"),sQuery(id+"F12.wireOp",EDGE,"E55.right"),sQuery(id+"F12.wireOp",EDGE,"E56.filletArc"),sQuery(id+"F12.wireOp",EDGE,"E57.filletArc"),sQuery(id+"F12.wireOp",EDGE,"E58.filletArc"),sQuery(id+"F12.wireOp",EDGE,"E59.filletArc"),sQuery(id+"F12.wireOp",EDGE,"E60.trimOffspring"),sQuery(id+"F12.wireOp",EDGE,"E61.trimOffspring"),sQuery(id+"F12.wireOp",EDGE,"E62.0"),sQuery(id+"F12.wireOp",EDGE,"E63.0")])],"isStart":false})]})});}
            var sketch = newSketch(context, id + "F23", { "sketchPlane" : qUnion([Q0])});
            skPoint(sketch, "E111.firstSnap0", {"position": v(-32.3, 1.4) * mm});
            skLineSegment(sketch, "E111.bottom", {"start": v(-33.62, 1.4) * mm, "end": v(33.36, 1.4) * mm});
            skLineSegment(sketch, "E111.top", {"start": v(-33.62, 3) * mm, "end": v(33.36, 3) * mm});
            skLineSegment(sketch, "E111.left", {"start": v(-33.62, 1.4) * mm, "end": v(-33.62, 3) * mm});
            skLineSegment(sketch, "E111.right", {"start": v(33.36, 1.4) * mm, "end": v(33.36, 3) * mm});
            skSolve(sketch);
        }
        {
            var Q0;
            Q0 = qSketchRegion(id + "F23", true);
            var Q1;
            {var subQ0=sQuery(id+"F0.wireOp",EDGE,"E4.filletArc");var subQ1=sQuery(id+"F0.wireOp",EDGE,"E3.filletArc");var subQ2=sQuery(id+"F0.wireOp",EDGE,"E2.filletArc");var subQ3=sQuery(id+"F0.wireOp",EDGE,"E1.filletArc");var subQ4=sQuery(id+"F0.wireOp",EDGE,"E0.bottom");var subQ5=sQuery(id+"F0.wireOp",EDGE,"E0.right");var subQ6=sQuery(id+"F0.wireOp",EDGE,"E0.top");var subQ7=sQuery(id+"F0.wireOp",EDGE,"E0.left");Q1=makeQuery(id+"F3.boolean.opBoolean","SPLIT",FACE,{"disambiguationData":[TD([makeQuery(id+"F1.opExtrude","SWEPT_FACE",FACE,{"disambiguationData":[OSD([subQ4])]})])],"derivedFrom":makeQuery(id+"F1.opExtrude","CAP_FACE",FACE,{"disambiguationData":[OSD([subQ4,subQ6,subQ7,subQ5,subQ3,subQ2,subQ1,subQ0])],"isStart":false})});}
            extrude(context, id + "F24", {"entities" : qUnion([Q0]), "operationType" : NewBodyOperationType.REMOVE, "endBound" : BoundingType.UP_TO_SURFACE, "oppositeDirection" : true, "endBoundEntityFace" : qUnion([Q1]), "depth" : 25 * mm});
        }
        {
            var Q0;
            Q0=makeQuery(id+"F17.boolean.opBoolean","COPY",FACE,{"derivedFrom":makeQuery(id+"F17.opExtrude","CAP_FACE",FACE,{"disambiguationData":[OSD([sQuery(id+"F16.wireOp",EDGE,"E81.bottom"),sQuery(id+"F16.wireOp",EDGE,"E81.top"),sQuery(id+"F16.wireOp",EDGE,"E81.left"),sQuery(id+"F16.wireOp",EDGE,"E81.right"),sQuery(id+"F16.wireOp",EDGE,"E82.filletArc"),sQuery(id+"F16.wireOp",EDGE,"E83.filletArc"),sQuery(id+"F16.wireOp",EDGE,"E84.filletArc"),sQuery(id+"F16.wireOp",EDGE,"E85.filletArc")])],"isStart":false})});
            var sketch = newSketch(context, id + "F25", { "sketchPlane" : qUnion([Q0])});
            skLineSegment(sketch, "E112.bottom", {"start": v(42.5, 27.5) * mm, "end": v(-42.5, 27.5) * mm});
            skLineSegment(sketch, "E112.top", {"start": v(42.5, -27.5) * mm, "end": v(-42.5, -27.5) * mm});
            skLineSegment(sketch, "E112.left", {"start": v(47.5, 22.5) * mm, "end": v(47.5, -22.5) * mm});
            skLineSegment(sketch, "E112.right", {"start": v(-47.5, 22.5) * mm, "end": v(-47.5, -22.5) * mm});
            skPoint(sketch, "E112.middle", {"position": v(0, 0) * mm});
            skPoint(sketch, "E113.visualSharp", {"position": v(-47.5, -27.5) * mm});
            skArc(sketch, "E113.filletArc", {"start": v(-47.5, -22.5) * mm, "mid": v(-46.04, -26.04) * mm, "end": v(-42.5, -27.5) * mm});
            skPoint(sketch, "E114.visualSharp", {"position": v(47.5, -27.5) * mm});
            skArc(sketch, "E114.filletArc", {"start": v(42.5, -27.5) * mm, "mid": v(46.04, -26.04) * mm, "end": v(47.5, -22.5) * mm});
            skPoint(sketch, "E115.visualSharp", {"position": v(47.5, 27.5) * mm});
            skArc(sketch, "E115.filletArc", {"start": v(47.5, 22.5) * mm, "mid": v(46.04, 26.04) * mm, "end": v(42.5, 27.5) * mm});
            skPoint(sketch, "E116.visualSharp", {"position": v(-47.5, 27.5) * mm});
            skArc(sketch, "E116.filletArc", {"start": v(-42.5, 27.5) * mm, "mid": v(-46.04, 26.04) * mm, "end": v(-47.5, 22.5) * mm});
            skSolve(sketch);
        }
        {
            var Q0;
            Q0 = qSketchRegion(id + "F25", true);
            extrude(context, id + "F26", {"entities" : qUnion([Q0]), "depth" : 2 * mm, "offsetDistance" : 25 * mm});
        }
        {
            var Q0;
            Q0=makeQuery(id+"F26.opExtrude","CAP_FACE",FACE,{"disambiguationData":[OSD([sQuery(id+"F25.wireOp",EDGE,"E112.bottom"),sQuery(id+"F25.wireOp",EDGE,"E112.top"),sQuery(id+"F25.wireOp",EDGE,"E112.left"),sQuery(id+"F25.wireOp",EDGE,"E112.right"),sQuery(id+"F25.wireOp",EDGE,"E113.filletArc"),sQuery(id+"F25.wireOp",EDGE,"E114.filletArc"),sQuery(id+"F25.wireOp",EDGE,"E115.filletArc"),sQuery(id+"F25.wireOp",EDGE,"E116.filletArc")])],"isStart":false});
            var sketch = newSketch(context, id + "F27", { "sketchPlane" : qUnion([Q0])});
            skCircle(sketch, "E117", {"center": v(-25, 0) * mm, "radius": 8 * mm});
            skSolve(sketch);
        }
        {
            var Q0;
            Q0=makeQuery(id+"F27.imprint","IMPRINT",FACE,{"disambiguationData":[TD([[makeQuery(id+"F27.imprint","IMPRINT",EDGE,{"derivedFrom":sQuery(id+"F27.wireOp",EDGE,"E117")}),1.0]])]});
            extrude(context, id + "F28", {"entities" : qUnion([Q0]), "operationType" : NewBodyOperationType.REMOVE, "endBound" : BoundingType.UP_TO_NEXT, "oppositeDirection" : true, "depth" : 25 * mm, "offsetDistance" : 25 * mm});
        }
    });
